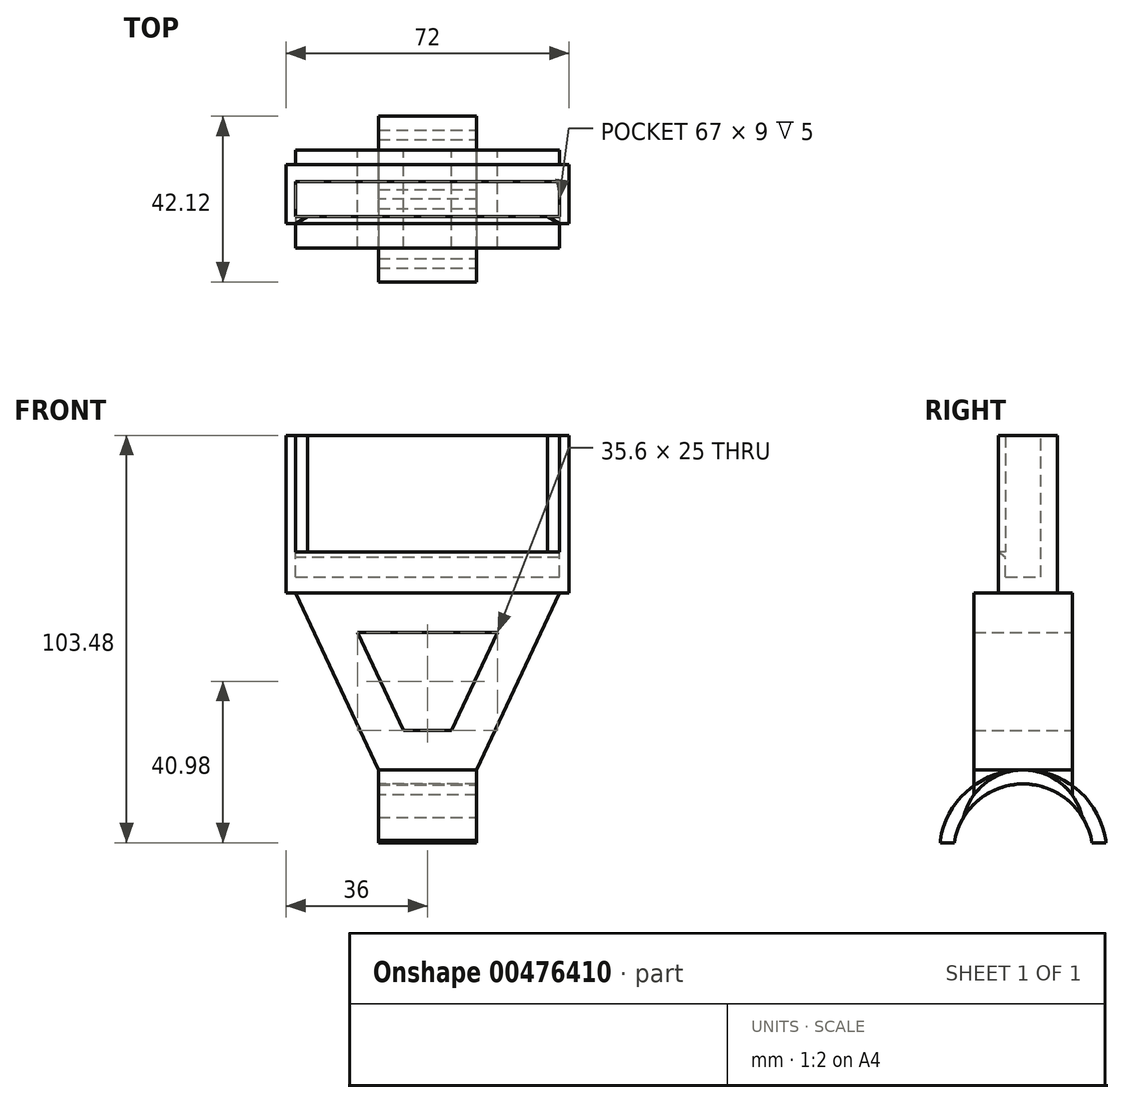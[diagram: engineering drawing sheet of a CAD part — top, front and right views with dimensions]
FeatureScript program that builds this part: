
annotation { "Feature Type Name" : "Feature", "Feature Type Description" : "" }
export const myFeature = defineFeature(function(context is Context, id is Id, definition is map)
    precondition{}
    {
        {
            var Q0;
            Q0=qCreatedBy(makeId("Right.planeOp"),FACE);
            var sketch = newSketch(context, id + "F0", { "sketchPlane" : qUnion([Q0])});
            skArc(sketch, "E0", {"start": v(14.97, -4.01) * mm, "mid": v(0, 15.5) * mm, "end": v(-14.97, -4.01) * mm});
            skLineSegment(sketch, "E1", {"start": v(-11.6, -3.1) * mm, "end": v(-14.97, -4.01) * mm});
            skLineSegment(sketch, "E2", {"start": v(11.6, -3.1) * mm, "end": v(14.97, -4.01) * mm});
            skArc(sketch, "E3.0", {"start": v(11.6, -3.1) * mm, "mid": v(0, 12) * mm, "end": v(-11.6, -3.1) * mm});
            skSolve(sketch);
        }
        {
            var Q0;
            Q0 = qSketchRegion(id + "F0", true);
            extrude(context, id + "F1", {"entities" : qUnion([Q0]), "endBound" : BoundingType.SYMMETRIC, "depth" : 25 * mm});
        }
        {
            var Q0;
            Q0=qCreatedBy(makeId("Front.planeOp"),FACE);
            var sketch = newSketch(context, id + "F2", { "sketchPlane" : qUnion([Q0])});
            skLineSegment(sketch, "E4", {"start": v(0, 0) * mm, "end": v(-12.5, 0) * mm});
            skLineSegment(sketch, "E5", {"start": v(-12.5, 0) * mm, "end": v(-12.5, 15.5) * mm});
            skLineSegment(sketch, "E6", {"start": v(-12.5, 15.5) * mm, "end": v(-33.5, 60.5) * mm});
            skLineSegment(sketch, "E7", {"start": v(-33.5, 60.5) * mm, "end": v(33.5, 60.5) * mm});
            skLineSegment(sketch, "E8", {"start": v(0, 0) * mm, "end": v(12.5, 0) * mm});
            skLineSegment(sketch, "E9", {"start": v(12.5, 0) * mm, "end": v(12.5, 15.5) * mm});
            skLineSegment(sketch, "E10", {"start": v(12.5, 15.5) * mm, "end": v(33.5, 60.5) * mm});
            skLineSegment(sketch, "E11", {"start": v(-33.5, 60.5) * mm, "end": v(0, 60.5) * mm});
            skLineSegment(sketch, "E12", {"start": v(-12.5, 15.5) * mm, "end": v(12.5, 15.5) * mm});
            skLineSegment(sketch, "E13.0", {"start": v(-6.13, 25.5) * mm, "end": v(-17.8, 50.5) * mm});
            skLineSegment(sketch, "E13.1", {"start": v(-6.13, 25.5) * mm, "end": v(6.13, 25.5) * mm});
            skLineSegment(sketch, "E13.2", {"start": v(6.13, 25.5) * mm, "end": v(17.8, 50.5) * mm});
            skLineSegment(sketch, "E13.3", {"start": v(-17.8, 50.5) * mm, "end": v(17.8, 50.5) * mm});
            skSolve(sketch);
        }
        {
            var Q0;
            Q0=makeQuery(id+"F2.imprint","IMPRINT",FACE,{"disambiguationData":[TD([[makeQuery(id+"F2.imprint","IMPRINT",EDGE,{"derivedFrom":sQuery(id+"F2.wireOp",EDGE,"E6")}),-1.0]])]});
            extrude(context, id + "F3", {"entities" : qUnion([Q0]), "endBound" : BoundingType.SYMMETRIC, "depth" : 25 * mm});
        }
        {
            var Q0;
            Q0=makeQuery(id+"F1.opExtrude","CAP_FACE",FACE,{"disambiguationData":[OSD([sQuery(id+"F0.wireOp",EDGE,"E0"),sQuery(id+"F0.wireOp",EDGE,"E1"),sQuery(id+"F0.wireOp",EDGE,"E2"),sQuery(id+"F0.wireOp",EDGE,"E3.0")])],"isStart":true});
            var sketch = newSketch(context, id + "F4", { "sketchPlane" : qUnion([Q0])});
            skLineSegment(sketch, "E14", {"start": v(0, 15.5) * mm, "end": v(-12.5, 15.5) * mm});
            skLineSegment(sketch, "E15", {"start": v(-12.5, 15.5) * mm, "end": v(-12.5, 9.17) * mm});
            skArc(sketch, "E16", {"start": v(0, 15.5) * mm, "mid": v(-7, 13.83) * mm, "end": v(-12.5, 9.17) * mm});
            skLineSegment(sketch, "E17", {"start": v(0, 15.5) * mm, "end": v(12.5, 15.5) * mm});
            skLineSegment(sketch, "E18", {"start": v(12.5, 15.5) * mm, "end": v(12.5, 9.17) * mm});
            skArc(sketch, "E19", {"start": v(12.5, 9.17) * mm, "mid": v(7, 13.83) * mm, "end": v(0, 15.5) * mm});
            skSolve(sketch);
        }
        {
            var Q0;
            Q0 = qSketchRegion(id + "F4", true);
            extrude(context, id + "F5", {"entities" : qUnion([Q0]), "oppositeDirection" : true, "depth" : 25 * mm});
        }
        {
            var Q0;
            Q0=makeQuery(id+"F3.opExtrude","SWEPT_FACE",FACE,{"disambiguationData":[OSD([sQuery(id+"F2.wireOp",EDGE,"E7"),sQuery(id+"F2.wireOp",EDGE,"E11")])]});
            var sketch = newSketch(context, id + "F6", { "sketchPlane" : qUnion([Q0])});
            skLineSegment(sketch, "E20.bottom", {"start": v(-36, 4.5) * mm, "end": v(36, 4.5) * mm});
            skLineSegment(sketch, "E20.top", {"start": v(-36, -4.5) * mm, "end": v(36, -4.5) * mm});
            skLineSegment(sketch, "E20.left", {"start": v(-36, 4.5) * mm, "end": v(-36, -4.5) * mm});
            skLineSegment(sketch, "E20.right", {"start": v(36, 4.5) * mm, "end": v(36, -4.5) * mm});
            skPoint(sketch, "E20.middle", {"position": v(0, 0) * mm});
            skSolve(sketch);
        }
        {
            var Q0;
            Q0 = qSketchRegion(id + "F6", true);
            extrude(context, id + "F7", {"entities" : qUnion([Q0]), "operationType" : NewBodyOperationType.ADD, "depth" : 4 * mm});
        }
        {
            var Q0;
            Q0=makeQuery(id+"F7.opExtrude","SWEPT_FACE",FACE,{"disambiguationData":[OSD([sQuery(id+"F6.wireOp",EDGE,"E20.left")])]});
            var sketch = newSketch(context, id + "F8", { "sketchPlane" : qUnion([Q0])});
            skLineSegment(sketch, "E21", {"start": v(4.5, 64.5) * mm, "end": v(4.5, 69.5) * mm});
            skLineSegment(sketch, "E22", {"start": v(4.5, 69.5) * mm, "end": v(6.22, 70.95) * mm});
            skLineSegment(sketch, "E23", {"start": v(6.22, 70.95) * mm, "end": v(6.22, 60.5) * mm});
            skLineSegment(sketch, "E24", {"start": v(6.22, 60.5) * mm, "end": v(4.5, 60.5) * mm});
            skLineSegment(sketch, "E25", {"start": v(4.5, 60.5) * mm, "end": v(4.5, 64.5) * mm});
            skSolve(sketch);
        }
        {
            var Q0;
            Q0 = qSketchRegion(id + "F8", true);
            extrude(context, id + "F9", {"entities" : qUnion([Q0]), "operationType" : NewBodyOperationType.ADD, "oppositeDirection" : true, "depth" : 72 * mm});
        }
        {
            var Q0;
            Q0=makeQuery(id+"F9.opExtrude","SWEPT_FACE",FACE,{"disambiguationData":[OSD([sQuery(id+"F8.wireOp",EDGE,"E23")])]});
            var sketch = newSketch(context, id + "F10", { "sketchPlane" : qUnion([Q0])});
            skLineSegment(sketch, "E26", {"start": v(-36, 60.5) * mm, "end": v(-33.5, 60.5) * mm});
            skLineSegment(sketch, "E27", {"start": v(-33.5, 60.5) * mm, "end": v(-33.5, 70.95) * mm});
            skLineSegment(sketch, "E28", {"start": v(-33.5, 70.95) * mm, "end": v(-36, 70.95) * mm});
            skLineSegment(sketch, "E29", {"start": v(-36, 70.95) * mm, "end": v(-36, 60.5) * mm});
            skLineSegment(sketch, "E30", {"start": v(36, 60.5) * mm, "end": v(33.5, 60.5) * mm});
            skLineSegment(sketch, "E31", {"start": v(33.5, 60.5) * mm, "end": v(33.5, 70.95) * mm});
            skLineSegment(sketch, "E32", {"start": v(33.5, 70.95) * mm, "end": v(36, 70.95) * mm});
            skLineSegment(sketch, "E33", {"start": v(36, 70.95) * mm, "end": v(36, 60.5) * mm});
            skSolve(sketch);
        }
        {
            var Q0;
            Q0 = qSketchRegion(id + "F10", true);
            var Q1;
            Q1=makeQuery(id+"F7.opExtrude","SWEPT_FACE",FACE,{"disambiguationData":[OSD([sQuery(id+"F6.wireOp",EDGE,"E20.bottom")])]});
            extrude(context, id + "F11", {"entities" : qUnion([Q0]), "operationType" : NewBodyOperationType.ADD, "endBound" : BoundingType.UP_TO_SURFACE, "oppositeDirection" : true, "endBoundEntityFace" : qUnion([Q1]), "depth" : 10.7 * mm});
        }
        {
            var Q0;
            Q0=makeQuery(id+"F11.boolean.opBoolean","MERGE",FACE,{"derivedFrom":[makeQuery(id+"F9.boolean.opBoolean","MERGE",FACE,{"derivedFrom":[makeQuery(id+"F7.opExtrude","SWEPT_FACE",FACE,{"disambiguationData":[OSD([sQuery(id+"F6.wireOp",EDGE,"E20.left")])]}),makeQuery(id+"F9.opExtrude","CAP_FACE",FACE,{"disambiguationData":[OSD([sQuery(id+"F8.wireOp",EDGE,"E21"),sQuery(id+"F8.wireOp",EDGE,"E22"),sQuery(id+"F8.wireOp",EDGE,"E23"),sQuery(id+"F8.wireOp",EDGE,"E24"),sQuery(id+"F8.wireOp",EDGE,"E25")])],"isStart":true})]}),makeQuery(id+"F11.opExtrude","SWEPT_FACE",FACE,{"disambiguationData":[OSD([sQuery(id+"F10.wireOp",EDGE,"E29")])]})]});
            var sketch = newSketch(context, id + "F12", { "sketchPlane" : qUnion([Q0])});
            skLineSegment(sketch, "E34.bottom", {"start": v(-4.5, 60.5) * mm, "end": v(-8.75, 60.5) * mm});
            skLineSegment(sketch, "E34.top", {"start": v(-4.5, 100.5) * mm, "end": v(-8.75, 100.5) * mm});
            skLineSegment(sketch, "E34.left", {"start": v(-4.5, 60.5) * mm, "end": v(-4.5, 100.5) * mm});
            skLineSegment(sketch, "E34.right", {"start": v(-8.75, 60.5) * mm, "end": v(-8.75, 100.5) * mm});
            skSolve(sketch);
        }
        {
            var Q0;
            Q0 = qSketchRegion(id + "F12", true);
            var Q1;
            Q1=makeQuery(id+"F11.boolean.opBoolean","MERGE",FACE,{"derivedFrom":[makeQuery(id+"F9.boolean.opBoolean","MERGE",FACE,{"derivedFrom":[makeQuery(id+"F7.opExtrude","SWEPT_FACE",FACE,{"disambiguationData":[OSD([sQuery(id+"F6.wireOp",EDGE,"E20.right")])]}),makeQuery(id+"F9.opExtrude","CAP_FACE",FACE,{"disambiguationData":[OSD([sQuery(id+"F8.wireOp",EDGE,"E21"),sQuery(id+"F8.wireOp",EDGE,"E22"),sQuery(id+"F8.wireOp",EDGE,"E23"),sQuery(id+"F8.wireOp",EDGE,"E24"),sQuery(id+"F8.wireOp",EDGE,"E25")])],"isStart":false})]}),makeQuery(id+"F11.opExtrude","SWEPT_FACE",FACE,{"disambiguationData":[OSD([sQuery(id+"F10.wireOp",EDGE,"E33")])]})]});
            extrude(context, id + "F13", {"entities" : qUnion([Q0]), "operationType" : NewBodyOperationType.ADD, "endBound" : BoundingType.UP_TO_SURFACE, "oppositeDirection" : true, "endBoundEntityFace" : qUnion([Q1]), "depth" : 25 * mm});
        }
        {
            var Q0;
            Q0=makeQuery(id+"F11.opExtrude","SWEPT_FACE",FACE,{"disambiguationData":[OSD([sQuery(id+"F10.wireOp",EDGE,"E28")])]});
            var sketch = newSketch(context, id + "F14", { "sketchPlane" : qUnion([Q0])});
            skLineSegment(sketch, "E35", {"start": v(-33.5, -6.22) * mm, "end": v(-30.52, -4.5) * mm});
            skLineSegment(sketch, "E36", {"start": v(-30.52, -4.5) * mm, "end": v(-33.5, -4.5) * mm});
            skLineSegment(sketch, "E37", {"start": v(-36, 4.5) * mm, "end": v(-33.5, 4.5) * mm});
            skLineSegment(sketch, "E38", {"start": v(-33.5, 4.5) * mm, "end": v(-33.5, -4.5) * mm});
            skLineSegment(sketch, "E39", {"start": v(-33.5, -6.22) * mm, "end": v(-36, -6.22) * mm});
            skLineSegment(sketch, "E40", {"start": v(-36, -6.22) * mm, "end": v(-36, 4.5) * mm});
            skSolve(sketch);
        }
        {
            var Q0;
            Q0 = qSketchRegion(id + "F14", true);
            var Q1;
            Q1=makeQuery(id+"F13.opExtrude","SWEPT_FACE",FACE,{"disambiguationData":[OSD([sQuery(id+"F12.wireOp",EDGE,"E34.top")])]});
            extrude(context, id + "F15", {"entities" : qUnion([Q0]), "operationType" : NewBodyOperationType.ADD, "endBound" : BoundingType.UP_TO_SURFACE, "endBoundEntityFace" : qUnion([Q1]), "depth" : 25 * mm});
        }
        {
            var Q0;
            Q0=makeQuery(id+"F11.opExtrude","SWEPT_FACE",FACE,{"disambiguationData":[OSD([sQuery(id+"F10.wireOp",EDGE,"E32")])]});
            var sketch = newSketch(context, id + "F16", { "sketchPlane" : qUnion([Q0])});
            skLineSegment(sketch, "E41", {"start": v(33.5, 4.5) * mm, "end": v(36, 4.5) * mm});
            skLineSegment(sketch, "E42", {"start": v(36, 4.5) * mm, "end": v(36, -6.22) * mm});
            skLineSegment(sketch, "E43", {"start": v(36, -6.22) * mm, "end": v(33.5, -6.22) * mm});
            skLineSegment(sketch, "E44", {"start": v(33.5, -6.22) * mm, "end": v(30.52, -4.5) * mm});
            skLineSegment(sketch, "E45", {"start": v(30.52, -4.5) * mm, "end": v(33.5, -4.5) * mm});
            skLineSegment(sketch, "E46", {"start": v(33.5, -4.5) * mm, "end": v(33.5, 4.5) * mm});
            skSolve(sketch);
        }
        {
            var Q0;
            Q0 = qSketchRegion(id + "F16", true);
            var Q1;
            {var subQ0=sQuery(id+"F12.wireOp",EDGE,"E34.top");Q1=makeQuery(id+"F15.boolean.opBoolean","MERGE",FACE,{"derivedFrom":[makeQuery(id+"F13.opExtrude","SWEPT_FACE",FACE,{"disambiguationData":[OSD([subQ0])]}),makeQuery(id+"F15.opExtrude","CAP_FACE",FACE,{"disambiguationData":[OSD([subQ0])],"isStart":false})]});}
            extrude(context, id + "F17", {"entities" : qUnion([Q0]), "operationType" : NewBodyOperationType.ADD, "endBound" : BoundingType.UP_TO_SURFACE, "endBoundEntityFace" : qUnion([Q1]), "depth" : 25 * mm});
        }
        {
            var Q0;
            Q0=makeQuery(id+"F1.opExtrude","CAP_FACE",FACE,{"disambiguationData":[OSD([sQuery(id+"F0.wireOp",EDGE,"E0"),sQuery(id+"F0.wireOp",EDGE,"E1"),sQuery(id+"F0.wireOp",EDGE,"E2"),sQuery(id+"F0.wireOp",EDGE,"E3.0")])],"isStart":false});
            var sketch = newSketch(context, id + "F18", { "sketchPlane" : qUnion([Q0])});
            skArc(sketch, "E47", {"start": v(11.6, -3.1) * mm, "mid": v(0, 12) * mm, "end": v(-11.6, -3.1) * mm});
            skArc(sketch, "E48", {"start": v(17.5, -2.98) * mm, "mid": v(0, 11.98) * mm, "end": v(-17.5, -2.98) * mm});
            skArc(sketch, "E49.0", {"start": v(21.06, -2.42) * mm, "mid": v(0, 15.58) * mm, "end": v(-21.06, -2.42) * mm});
            skLineSegment(sketch, "E50", {"start": v(-17.5, -2.98) * mm, "end": v(-21.06, -2.98) * mm});
            skLineSegment(sketch, "E51", {"start": v(-21.06, -2.98) * mm, "end": v(-21.06, -2.42) * mm});
            skLineSegment(sketch, "E52", {"start": v(17.5, -2.98) * mm, "end": v(21.06, -2.98) * mm});
            skLineSegment(sketch, "E53", {"start": v(21.06, -2.98) * mm, "end": v(21.06, -2.42) * mm});
            skSolve(sketch);
        }
        {
            var Q0;
            Q0 = qSketchRegion(id + "F18", true);
            extrude(context, id + "F19", {"entities" : qUnion([Q0]), "oppositeDirection" : true, "depth" : 25 * mm});
        }
        {
            var Q0;
            Q0=makeQuery(id+"F19.opExtrude","CAP_FACE",FACE,{"disambiguationData":[OSD([sQuery(id+"F18.wireOp",EDGE,"E48"),sQuery(id+"F18.wireOp",EDGE,"E49.0"),sQuery(id+"F18.wireOp",EDGE,"E50"),sQuery(id+"F18.wireOp",EDGE,"E51"),sQuery(id+"F18.wireOp",EDGE,"E52"),sQuery(id+"F18.wireOp",EDGE,"E53")])],"isStart":true});
            var sketch = newSketch(context, id + "F20", { "sketchPlane" : qUnion([Q0])});
            skArc(sketch, "E54", {"start": v(17.5, -2.98) * mm, "mid": v(0, 11.92) * mm, "end": v(-17.5, -2.98) * mm});
            skLineSegment(sketch, "E55", {"start": v(-17.5, -2.98) * mm, "end": v(0.34, -12.67) * mm});
            skLineSegment(sketch, "E56", {"start": v(0.34, -12.67) * mm, "end": v(17.5, -2.98) * mm});
            skSolve(sketch);
        }
        {
            var Q0;
            Q0 = qSketchRegion(id + "F20", true);
            extrude(context, id + "F21", {"entities" : qUnion([Q0]), "operationType" : NewBodyOperationType.REMOVE, "oppositeDirection" : true, "depth" : 25 * mm});
        }
    });
